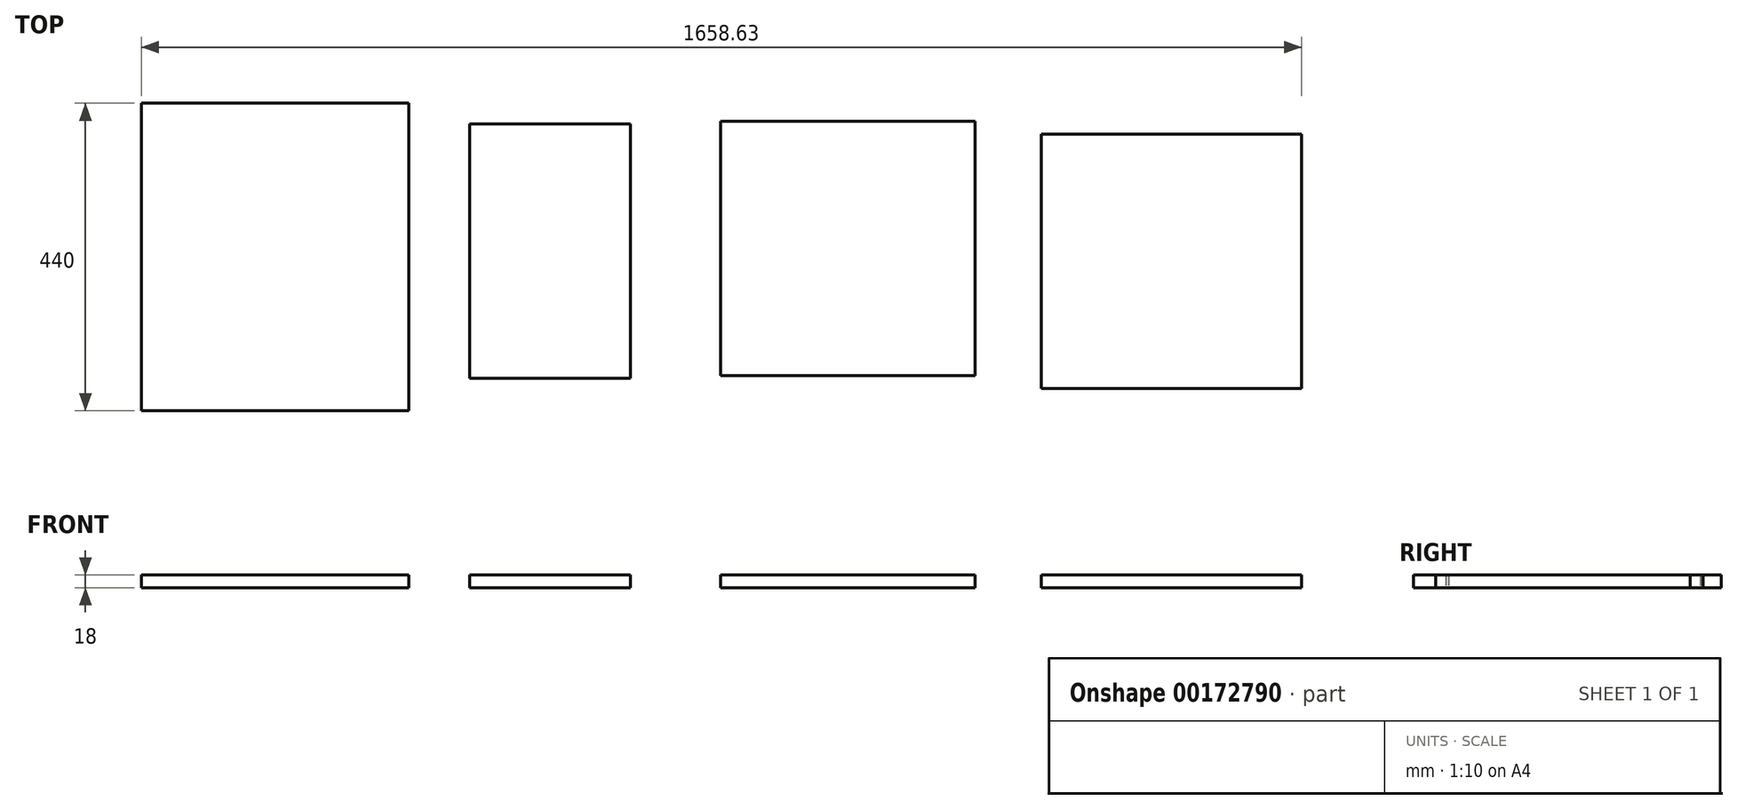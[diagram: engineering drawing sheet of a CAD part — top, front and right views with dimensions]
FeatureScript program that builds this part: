
annotation { "Feature Type Name" : "Feature", "Feature Type Description" : "" }
export const myFeature = defineFeature(function(context is Context, id is Id, definition is map)
    precondition{}
    {
        {
            var Q0;
            Q0=qCreatedBy(makeId("Top.planeOp"),FACE);
            var sketch = newSketch(context, id + "F0", { "sketchPlane" : qUnion([Q0])});
            skLineSegment(sketch, "E0.bottom", {"start": v(-348.42, 403.36) * mm, "end": v(33.58, 403.36) * mm});
            skLineSegment(sketch, "E0.top", {"start": v(-348.42, -36.64) * mm, "end": v(33.58, -36.64) * mm});
            skLineSegment(sketch, "E0.left", {"start": v(-348.42, 403.36) * mm, "end": v(-348.42, -36.64) * mm});
            skLineSegment(sketch, "E0.right", {"start": v(33.58, 403.36) * mm, "end": v(33.58, -36.64) * mm});
            skLineSegment(sketch, "E1.bottom", {"start": v(121.08, 373.91) * mm, "end": v(351.08, 373.91) * mm});
            skLineSegment(sketch, "E1.top", {"start": v(121.08, 9.91) * mm, "end": v(351.08, 9.91) * mm});
            skLineSegment(sketch, "E1.left", {"start": v(121.08, 373.91) * mm, "end": v(121.08, 9.91) * mm});
            skLineSegment(sketch, "E1.right", {"start": v(351.08, 373.91) * mm, "end": v(351.08, 9.91) * mm});
            skLineSegment(sketch, "E2.bottom", {"start": v(479.48, 377.48) * mm, "end": v(843.48, 377.48) * mm});
            skLineSegment(sketch, "E2.top", {"start": v(479.48, 13.48) * mm, "end": v(843.48, 13.48) * mm});
            skLineSegment(sketch, "E2.left", {"start": v(479.48, 377.48) * mm, "end": v(479.48, 13.48) * mm});
            skLineSegment(sketch, "E2.right", {"start": v(843.48, 377.48) * mm, "end": v(843.48, 13.48) * mm});
            skLineSegment(sketch, "E3.bottom", {"start": v(938.2, 358.97) * mm, "end": v(1310.2, 358.97) * mm});
            skLineSegment(sketch, "E3.top", {"start": v(938.2, -5.03) * mm, "end": v(1310.2, -5.03) * mm});
            skLineSegment(sketch, "E3.left", {"start": v(938.2, 358.97) * mm, "end": v(938.2, -5.03) * mm});
            skLineSegment(sketch, "E3.right", {"start": v(1310.2, 358.97) * mm, "end": v(1310.2, -5.03) * mm});
            skSolve(sketch);
        }
        {
            var Q0;
            Q0=makeQuery(id+"F0.imprint","IMPRINT",FACE,{"disambiguationData":[TD([[makeQuery(id+"F0.imprint","IMPRINT",EDGE,{"derivedFrom":sQuery(id+"F0.wireOp",EDGE,"E0.bottom")}),-1.0]])]});
            var Q1;
            Q1=makeQuery(id+"F0.imprint","IMPRINT",FACE,{"disambiguationData":[TD([[makeQuery(id+"F0.imprint","IMPRINT",EDGE,{"derivedFrom":sQuery(id+"F0.wireOp",EDGE,"E1.bottom")}),-1.0]])]});
            var Q2;
            Q2=makeQuery(id+"F0.imprint","IMPRINT",FACE,{"disambiguationData":[TD([[makeQuery(id+"F0.imprint","IMPRINT",EDGE,{"derivedFrom":sQuery(id+"F0.wireOp",EDGE,"E2.bottom")}),-1.0]])]});
            var Q3;
            Q3=makeQuery(id+"F0.imprint","IMPRINT",FACE,{"disambiguationData":[TD([[makeQuery(id+"F0.imprint","IMPRINT",EDGE,{"derivedFrom":sQuery(id+"F0.wireOp",EDGE,"E3.bottom")}),-1.0]])]});
            extrude(context, id + "F1", {"entities" : qUnion([Q0, Q1, Q2, Q3]), "depth" : 18 * mm});
        }
    });
